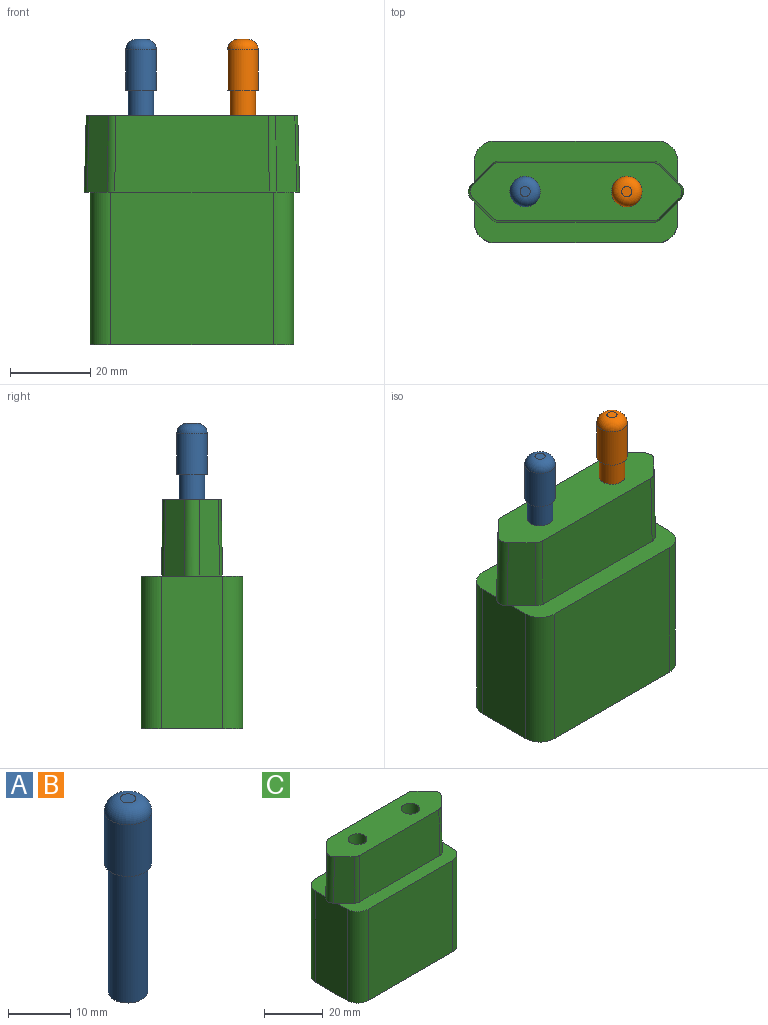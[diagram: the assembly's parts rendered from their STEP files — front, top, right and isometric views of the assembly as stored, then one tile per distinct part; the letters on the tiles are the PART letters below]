
ASSEMBLY  parts=3 mates=2
PART A: 6 faces, bbox 7.6x7.6x38.1 mm
  f0: cylinder r=3.17mm len=25.4mm, axis (0,0,-1), area 506.7mm2, adj f1,f3
  f1: plane 6.35x6.35mm, normal (0,0,-1), area 31.7mm2, adj f0
  f2: cylinder r=3.81mm len=10.16mm, axis (0,0,1), area 243.2mm2, adj f3,f5
  f3: plane 7.62x7.62mm, normal (0,0,-1), area 13.9mm2, adj f0,f2
  f4: plane 2.54x2.54mm, normal (0,0,1), area 5.1mm2, adj f5
  f5: torus R=1.27mm, axis (0,0,1), area 72.4mm2, adj f2,f4
PART B: same geometry as A
PART C: 40 faces, bbox 53.8x25.4x57.2 mm
  f0: plane 50.8x25.4mm, normal (0,0,-1), area 1113.3mm2, adj f3,f4,f5,f6,f7,f8,f9,f10
  f1: plane 50.81x10.17mm, normal (0,0,1), area 273.1mm2, adj f4,f5,f6,f8,f9,f12,f16,f17
  f2: plane 50.81x10.17mm, normal (0,0,1), area 273.1mm2, adj f3,f4,f6,f7,f10,f13,f14,f15
  f3: plane 40.64x38.1mm, normal (0,-1,0), area 1548.4mm2, adj f0,f2,f7,f10
  f4: plane 38.1x15.24mm, normal (1,0,0), area 580.6mm2, adj f0,f1,f2,f7,f8,f11
  f5: plane 40.64x38.1mm, normal (0,1,0), area 1548.4mm2, adj f0,f1,f8,f9
  f6: plane 38.1x15.24mm, normal (-1,0,0), area 580.6mm2, adj f0,f1,f2,f9,f10,f19
  f7: cylinder r=5.08mm len=38.1mm, axis (0,0,1), area 304mm2, adj f0,f2,f3,f4
  f8: cylinder r=5.08mm len=38.1mm, axis (0,0,-1), area 304mm2, adj f0,f1,f4,f5
  f9: cylinder r=5.08mm len=38.1mm, axis (0,0,1), area 304mm2, adj f0,f1,f5,f6
  f10: cylinder r=5.08mm len=38.1mm, axis (0,0,-1), area 304mm2, adj f0,f2,f3,f6
  f11: plane 5.08x1.49mm, normal (0,0,-1), area 5.1mm2, adj f4,f15,f16,f21
  f12: plane 19.05x5.22mm, normal (-0.71,0.71,0.02), area 132.4mm2, adj f1,f18,f19,f20,f25
  f13: plane 19.05x5.22mm, normal (-0.71,-0.71,0.02), area 132.4mm2, adj f2,f18,f19,f20,f22
  f14: plane 38.54x19.05mm, normal (0,-1,0.02), area 731.6mm2, adj f2,f18,f22,f23
  f15: plane 19.05x5.22mm, normal (0.71,-0.71,0.02), area 132.4mm2, adj f2,f11,f18,f21,f23
  f16: plane 19.05x5.22mm, normal (0.71,0.71,0.02), area 132.4mm2, adj f1,f11,f18,f21,f24
  f17: plane 38.54x19.05mm, normal (0,1,0.02), area 731.6mm2, adj f1,f18,f24,f25
  f18: plane 52.84x14.58mm, normal (0,0,1), area 627.9mm2, adj f12,f13,f14,f15,f16,f17,f20,f21
  f19: plane 5.08x1.49mm, normal (0,0,-1), area 5.1mm2, adj f6,f12,f13,f20
  f20: cylinder r=2.54mm len=19.09mm, axis (-0.02,0,-1), area 76mm2, adj f12,f13,f18,f19
  f21: cylinder r=2.54mm len=19.09mm, axis (0.02,0,-1), area 76mm2, adj f11,f15,f16,f18
  f22: cylinder r=2.54mm len=19.05mm, axis (-0.01,-0.02,-1), area 38mm2, adj f2,f13,f14,f18
  f23: cylinder r=2.54mm len=19.05mm, axis (0.01,-0.02,-1), area 38mm2, adj f2,f14,f15,f18
  f24: cylinder r=2.54mm len=19.05mm, axis (0.01,0.02,-1), area 38mm2, adj f1,f16,f17,f18
  f25: cylinder r=2.54mm len=19.05mm, axis (-0.01,0.02,-1), area 38mm2, adj f1,f12,f17,f18
  f26: plane 6.35x6.35mm, normal (0,0,1), area 31.7mm2, adj f27
  f27: cylinder r=3.17mm len=19.05mm, axis (0,0,1), area 380mm2, adj f18,f26
  f28: plane 6.35x6.35mm, normal (0,0,1), area 31.7mm2, adj f29
  f29: cylinder r=3.17mm len=19.05mm, axis (0,0,1), area 380mm2, adj f18,f28
  f30: plane 15.24x12.7mm, normal (0,1,0), area 193.5mm2, adj f0,f31,f33,f34
  f31: plane 12.7x5.08mm, normal (1,0,0), area 64.5mm2, adj f0,f30,f32,f34
  f32: plane 15.24x12.7mm, normal (0,-1,0), area 193.5mm2, adj f0,f31,f33,f34
  f33: plane 12.7x5.08mm, normal (-1,0,0), area 64.5mm2, adj f0,f30,f32,f34
  f34: plane 15.24x5.08mm, normal (0,0,-1), area 77.4mm2, adj f30,f31,f32,f33
  f35: plane 15.24x12.7mm, normal (0,1,0), area 193.5mm2, adj f0,f36,f38,f39
  f36: plane 12.7x5.08mm, normal (1,0,0), area 64.5mm2, adj f0,f35,f37,f39
  f37: plane 15.24x12.7mm, normal (0,-1,0), area 193.5mm2, adj f0,f36,f38,f39
  f38: plane 12.7x5.08mm, normal (-1,0,0), area 64.5mm2, adj f0,f35,f37,f39
  f39: plane 15.24x5.08mm, normal (0,0,-1), area 77.4mm2, adj f35,f36,f37,f38
PLACE A t=(-5.43,14.8,66.71)mm
PLACE B t=(19.97,14.8,66.71)mm
PLACE C t=(7.27,14.8,28.61)mm
MATE fastened B.f0 <-> C.f27  axis (0,0,-1) through (19.97,14.8,66.71)mm
MATE fastened A.f0 <-> C.f29  axis (0,0,-1) through (-5.43,14.8,66.71)mm
